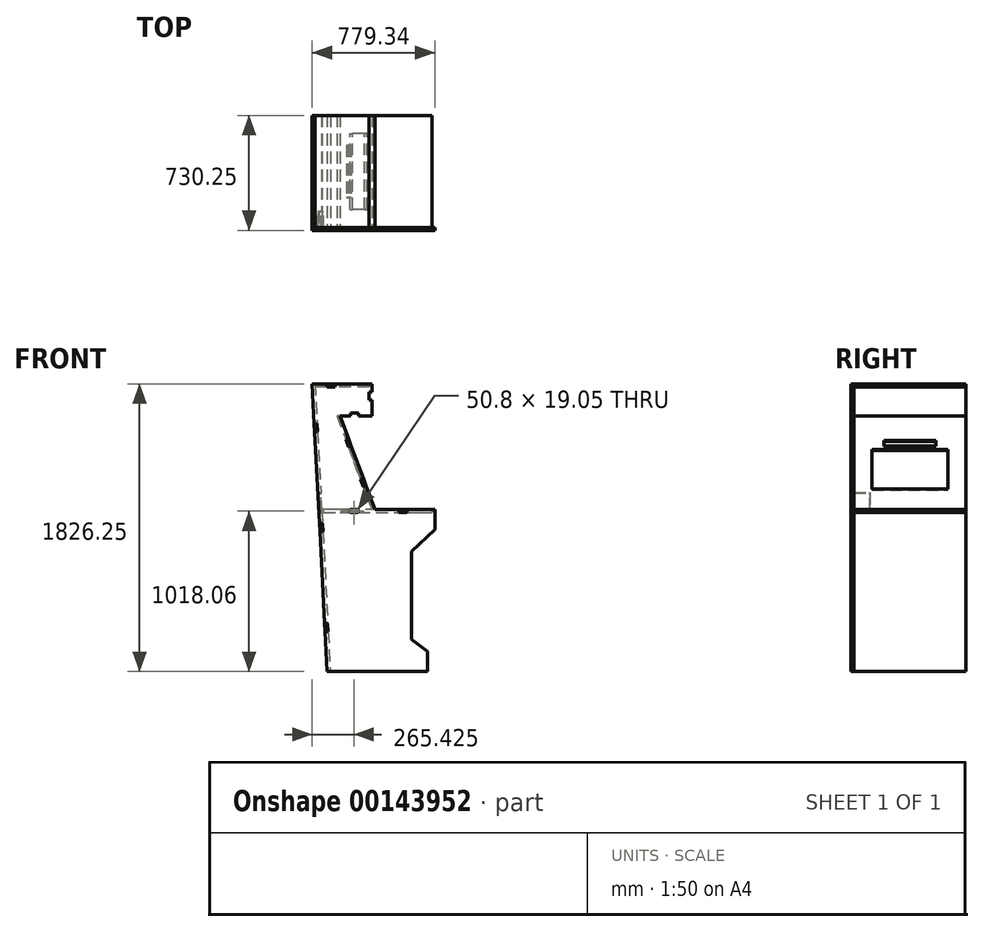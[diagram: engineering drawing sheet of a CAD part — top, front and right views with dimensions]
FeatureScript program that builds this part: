
annotation { "Feature Type Name" : "Feature", "Feature Type Description" : "" }
export const myFeature = defineFeature(function(context is Context, id is Id, definition is map)
    precondition{}
    {
        {
            var Q0;
            Q0=qCreatedBy(makeId("Front.planeOp"),FACE);
            var sketch = newSketch(context, id + "F0", { "sketchPlane" : qUnion([Q0])});
            skLineSegment(sketch, "E0.top", {"start": v(-166.11, 1576.37) * mm, "end": v(-343.91, 1576.37) * mm});
            skPoint(sketch, "E1.visualSharp", {"position": v(-407.41, 1576.37) * mm});
            skLineSegment(sketch, "E2", {"start": v(-247.51, -249.88) * mm, "end": v(387.49, -249.88) * mm});
            skLineSegment(sketch, "E3", {"start": v(387.49, -249.88) * mm, "end": v(387.49, -122.88) * mm});
            skLineSegment(sketch, "E4", {"start": v(387.49, -122.88) * mm, "end": v(286.3, -46.13) * mm});
            skLineSegment(sketch, "E5", {"start": v(286.3, -46.13) * mm, "end": v(286.3, 512.67) * mm});
            skLineSegment(sketch, "E6", {"start": v(286.3, 512.67) * mm, "end": v(435.43, 650.7) * mm});
            skLineSegment(sketch, "E7", {"start": v(435.43, 650.7) * mm, "end": v(435.43, 736.01) * mm});
            skLineSegment(sketch, "E8", {"start": v(435.43, 777.7) * mm, "end": v(54.43, 777.7) * mm});
            skLineSegment(sketch, "E9", {"start": v(54.43, 777.7) * mm, "end": v(-166.11, 1373.17) * mm});
            skLineSegment(sketch, "E10.bottom", {"start": v(-166.11, 1373.17) * mm, "end": v(37.09, 1373.17) * mm});
            skLineSegment(sketch, "E10.top", {"start": v(-166.11, 1576.37) * mm, "end": v(37.09, 1576.37) * mm});
            skLineSegment(sketch, "E10.right", {"start": v(37.09, 1373.17) * mm, "end": v(37.09, 1576.37) * mm});
            skLineSegment(sketch, "E11", {"start": v(-343.91, 1576.37) * mm, "end": v(-247.51, -249.88) * mm});
            skLineSegment(sketch, "E12", {"start": v(435.43, 736.01) * mm, "end": v(435.43, 777.7) * mm});
            skLineSegment(sketch, "E13", {"start": v(435.43, 650.7) * mm, "end": v(-295.05, 650.7) * mm, "construction": true});
            skSolve(sketch);
        }
        {
            var Q0;
            Q0=makeQuery(id+"F0.imprint","IMPRINT",FACE,{"disambiguationData":[TD([[makeQuery(id+"F0.imprint","IMPRINT",EDGE,{"derivedFrom":sQuery(id+"F0.wireOp",EDGE,"E0.top")}),1.0]])]});
            var sketch = newSketch(context, id + "F1", { "sketchPlane" : qUnion([Q0])});
            skSolve(sketch);
        }
        {
            var Q0;
            Q0=makeQuery(id+"F1.imprint","IMPRINT",FACE,{"disambiguationData":[TD([[makeQuery(id+"F1.imprint","IMPRINT",EDGE,{"derivedFrom":makeQuery(id+"F0.imprint","IMPRINT",EDGE,{"derivedFrom":sQuery(id+"F0.wireOp",EDGE,"E0.top")})}),1.0]])]});
            extrude(context, id + "F2", {"entities" : qUnion([Q0]), "depth" : 19.05 * mm});
        }
        {
            var Q0;
            Q0=makeQuery(id+"F0.imprint","IMPRINT",FACE,{"disambiguationData":[TD([[makeQuery(id+"F0.imprint","IMPRINT",EDGE,{"derivedFrom":sQuery(id+"F0.wireOp",EDGE,"E0.top")}),1.0]])]});
            var sketch = newSketch(context, id + "F3", { "sketchPlane" : qUnion([Q0])});
            skLineSegment(sketch, "E14.0.0", {"start": v(-58.16, 1576.37) * mm, "end": v(-108.96, 1576.37) * mm});
            skLineSegment(sketch, "E14.0.1", {"start": v(-196.83, 1576.37) * mm, "end": v(-247.63, 1576.37) * mm});
            skLineSegment(sketch, "E14.0.2", {"start": v(-330.53, 1322.73) * mm, "end": v(-327.85, 1272) * mm});
            skLineSegment(sketch, "E14.0.3", {"start": v(-247.51, -249.88) * mm, "end": v(387.49, -249.88) * mm});
            skLineSegment(sketch, "E14.0.4", {"start": v(387.49, -249.88) * mm, "end": v(387.49, -122.88) * mm});
            skLineSegment(sketch, "E14.0.5", {"start": v(387.49, -122.88) * mm, "end": v(286.3, -46.13) * mm});
            skLineSegment(sketch, "E14.0.6", {"start": v(286.3, -46.13) * mm, "end": v(286.3, 512.67) * mm});
            skLineSegment(sketch, "E14.0.7", {"start": v(286.3, 512.67) * mm, "end": v(435.43, 650.7) * mm});
            skLineSegment(sketch, "E14.0.8", {"start": v(435.43, 650.7) * mm, "end": v(435.43, 736.01) * mm});
            skLineSegment(sketch, "E14.0.9", {"start": v(435.43, 736.01) * mm, "end": v(435.43, 777.7) * mm});
            skLineSegment(sketch, "E14.0.10", {"start": v(257.63, 777.7) * mm, "end": v(206.83, 777.7) * mm});
            skLineSegment(sketch, "E14.0.11", {"start": v(-0.8, 926.82) * mm, "end": v(-18.44, 974.46) * mm});
            skLineSegment(sketch, "E14.0.12", {"start": v(-99.44, 1373.17) * mm, "end": v(-48.64, 1373.17) * mm});
            skLineSegment(sketch, "E14.0.13", {"start": v(37.09, 1474.77) * mm, "end": v(37.09, 1525.57) * mm});
            skPoint(sketch, "E15", {"position": v(18.04, 1557.32) * mm});
            skPoint(sketch, "E16", {"position": v(-323.83, 1557.32) * mm});
            skPoint(sketch, "E17", {"position": v(18.04, 1392.22) * mm});
            skPoint(sketch, "E18", {"position": v(-166.11, 1392.22) * mm});
            skPoint(sketch, "E19", {"position": v(-185.16, 1373.17) * mm});
            skPoint(sketch, "E20", {"position": v(35.38, 777.7) * mm});
            skPoint(sketch, "E21", {"position": v(-228.46, -249.88) * mm});
            skLineSegment(sketch, "E22", {"start": v(-323.83, 1557.32) * mm, "end": v(-228.46, -249.88) * mm, "construction": true});
            skLineSegment(sketch, "E23", {"start": v(-185.16, 1373.17) * mm, "end": v(35.38, 777.7) * mm, "construction": true});
            skLineSegment(sketch, "E24", {"start": v(18.04, 1557.32) * mm, "end": v(-323.83, 1557.32) * mm, "construction": true});
            skLineSegment(sketch, "E25", {"start": v(18.04, 1557.32) * mm, "end": v(18.04, 1392.22) * mm, "construction": true});
            skLineSegment(sketch, "E26", {"start": v(-166.11, 1392.22) * mm, "end": v(18.04, 1392.22) * mm, "construction": true});
            skLineSegment(sketch, "E27.top", {"start": v(-196.83, 1557.32) * mm, "end": v(-247.63, 1557.32) * mm});
            skLineSegment(sketch, "E27.left", {"start": v(-196.83, 1576.37) * mm, "end": v(-196.83, 1557.32) * mm});
            skLineSegment(sketch, "E27.right", {"start": v(-247.63, 1576.37) * mm, "end": v(-247.63, 1557.32) * mm});
            skLineSegment(sketch, "E28.bottom", {"start": v(-108.96, 1576.37) * mm, "end": v(-58.16, 1576.37) * mm});
            skLineSegment(sketch, "E28.top", {"start": v(-108.96, 1557.32) * mm, "end": v(-58.16, 1557.32) * mm});
            skLineSegment(sketch, "E28.left", {"start": v(-108.96, 1576.37) * mm, "end": v(-108.96, 1557.32) * mm});
            skLineSegment(sketch, "E28.right", {"start": v(-58.16, 1576.37) * mm, "end": v(-58.16, 1557.32) * mm});
            skLineSegment(sketch, "E29.bottom", {"start": v(-48.64, 1392.22) * mm, "end": v(-99.44, 1392.22) * mm});
            skLineSegment(sketch, "E29.top", {"start": v(-48.64, 1373.17) * mm, "end": v(-99.44, 1373.17) * mm});
            skLineSegment(sketch, "E29.left", {"start": v(-48.64, 1392.22) * mm, "end": v(-48.64, 1373.17) * mm});
            skLineSegment(sketch, "E29.right", {"start": v(-99.44, 1392.22) * mm, "end": v(-99.44, 1373.17) * mm});
            skLineSegment(sketch, "E30.bottom", {"start": v(37.09, 1525.57) * mm, "end": v(18.04, 1525.57) * mm});
            skLineSegment(sketch, "E30.top", {"start": v(37.09, 1474.77) * mm, "end": v(18.04, 1474.77) * mm});
            skLineSegment(sketch, "E30.left", {"start": v(37.09, 1525.57) * mm, "end": v(37.09, 1474.77) * mm});
            skLineSegment(sketch, "E30.right", {"start": v(18.04, 1525.57) * mm, "end": v(18.04, 1474.77) * mm});
            skPoint(sketch, "E31", {"position": v(-17.55, 920.61) * mm});
            skPoint(sketch, "E32", {"position": v(-35.2, 968.25) * mm});
            skPoint(sketch, "E33", {"position": v(-112.3, 1176.42) * mm});
            skPoint(sketch, "E34", {"position": v(-129.94, 1224.06) * mm});
            skLineSegment(sketch, "E35", {"start": v(-129.94, 1224.06) * mm, "end": v(-113.18, 1230.26) * mm});
            skLineSegment(sketch, "E36", {"start": v(-112.3, 1176.42) * mm, "end": v(-95.54, 1182.62) * mm});
            skLineSegment(sketch, "E37", {"start": v(-17.55, 920.61) * mm, "end": v(-0.8, 926.82) * mm});
            skLineSegment(sketch, "E38", {"start": v(-35.2, 968.25) * mm, "end": v(-18.44, 974.46) * mm});
            skLineSegment(sketch, "E39", {"start": v(-17.55, 920.61) * mm, "end": v(-35.2, 968.25) * mm});
            skLineSegment(sketch, "E40", {"start": v(-129.94, 1224.06) * mm, "end": v(-112.3, 1176.42) * mm});
            skPoint(sketch, "E41", {"position": v(-330.53, 1322.73) * mm});
            skPoint(sketch, "E42", {"position": v(-327.85, 1272) * mm});
            skPoint(sketch, "E43", {"position": v(-297.05, 688.6) * mm});
            skPoint(sketch, "E44", {"position": v(-294.38, 637.88) * mm});
            skPoint(sketch, "E45", {"position": v(-263.58, 54.5) * mm});
            skPoint(sketch, "E46", {"position": v(-260.9, 3.76) * mm});
            skLineSegment(sketch, "E47", {"start": v(-297.05, 688.6) * mm, "end": v(-278.04, 689.61) * mm});
            skLineSegment(sketch, "E48", {"start": v(-294.38, 637.88) * mm, "end": v(-275.37, 638.88) * mm});
            skLineSegment(sketch, "E49", {"start": v(-275.37, 638.88) * mm, "end": v(-278.04, 689.61) * mm});
            skLineSegment(sketch, "E50", {"start": v(-330.53, 1322.73) * mm, "end": v(-311.5, 1323.73) * mm});
            skLineSegment(sketch, "E51", {"start": v(-327.85, 1272) * mm, "end": v(-308.83, 1273) * mm});
            skLineSegment(sketch, "E52", {"start": v(-308.83, 1273) * mm, "end": v(-311.5, 1323.73) * mm});
            skLineSegment(sketch, "E53", {"start": v(-260.9, 3.76) * mm, "end": v(-241.9, 4.77) * mm});
            skLineSegment(sketch, "E54", {"start": v(-263.58, 54.5) * mm, "end": v(-244.58, 55.5) * mm});
            skLineSegment(sketch, "E55", {"start": v(-244.58, 55.5) * mm, "end": v(-241.9, 4.77) * mm});
            skLineSegment(sketch, "E56", {"start": v(514.5, 758.65) * mm, "end": v(-381.03, 758.65) * mm, "construction": true});
            skLineSegment(sketch, "E57.top", {"start": v(257.63, 758.65) * mm, "end": v(206.83, 758.65) * mm});
            skLineSegment(sketch, "E57.left", {"start": v(257.63, 777.7) * mm, "end": v(257.63, 758.65) * mm});
            skLineSegment(sketch, "E57.right", {"start": v(206.83, 777.7) * mm, "end": v(206.83, 758.65) * mm});
            skLineSegment(sketch, "E58.bottom", {"start": v(-103.89, 758.65) * mm, "end": v(-53.09, 758.65) * mm});
            skLineSegment(sketch, "E58.top", {"start": v(-103.89, 777.7) * mm, "end": v(-53.09, 777.7) * mm});
            skLineSegment(sketch, "E58.left", {"start": v(-103.89, 758.65) * mm, "end": v(-103.89, 777.7) * mm});
            skLineSegment(sketch, "E58.right", {"start": v(-53.09, 758.65) * mm, "end": v(-53.09, 777.7) * mm});
            skPoint(sketch, "E59", {"position": v(-281.69, 758.65) * mm});
            skLineSegment(sketch, "E60", {"start": v(-297.05, 688.6) * mm, "end": v(-294.38, 637.88) * mm});
            skPoint(sketch, "E61.orphan", {"position": v(54.43, 777.7) * mm});
            skLineSegment(sketch, "E62.trimOffspring", {"start": v(-95.54, 1182.62) * mm, "end": v(-113.18, 1230.26) * mm});
            skPoint(sketch, "E63.orphan", {"position": v(-166.11, 1373.17) * mm});
            skPoint(sketch, "E64.orphan", {"position": v(37.09, 1373.17) * mm});
            skPoint(sketch, "E65.orphan", {"position": v(37.09, 1576.37) * mm});
            skPoint(sketch, "E66.orphan", {"position": v(-166.11, 1576.37) * mm});
            skPoint(sketch, "E67.orphan", {"position": v(-343.91, 1576.37) * mm});
            skLineSegment(sketch, "E68.trimOffspring", {"start": v(-300.75, 758.65) * mm, "end": v(-294.38, 637.88) * mm});
            skLineSegment(sketch, "E69.trimOffspring", {"start": v(-263.58, 54.5) * mm, "end": v(-260.9, 3.76) * mm});
            skSolve(sketch);
        }
        {
            var Q0;
            Q0=makeQuery(id+"F3.imprint","IMPRINT",FACE,{"disambiguationData":[TD([[makeQuery(id+"F3.imprint","IMPRINT",EDGE,{"derivedFrom":sQuery(id+"F3.wireOp",EDGE,"E57.top")}),-1.0]])]});
            var Q1;
            Q1=makeQuery(id+"F3.imprint","IMPRINT",FACE,{"disambiguationData":[TD([[makeQuery(id+"F3.imprint","IMPRINT",EDGE,{"derivedFrom":sQuery(id+"F3.wireOp",EDGE,"E58.bottom")}),1.0]])]});
            var Q2;
            {var subQ0=sQuery(id+"F3.wireOp",EDGE,"E47");Q2=makeQuery(id+"F3.imprint","IMPRINT",FACE,{"disambiguationData":[TD([[makeQuery(id+"F3.imprint","IMPRINT",EDGE,{"derivedFrom":subQ0}),-1.0]])]});}
            var Q3;
            Q3=makeQuery(id+"F3.imprint","IMPRINT",FACE,{"disambiguationData":[TD([[makeQuery(id+"F3.imprint","IMPRINT",EDGE,{"derivedFrom":sQuery(id+"F3.wireOp",EDGE,"E14.0.11")}),1.0]])]});
            var Q4;
            Q4=makeQuery(id+"F3.imprint","IMPRINT",FACE,{"disambiguationData":[TD([[makeQuery(id+"F3.imprint","IMPRINT",EDGE,{"derivedFrom":sQuery(id+"F3.wireOp",EDGE,"E35")}),-1.0]])]});
            var Q5;
            Q5=makeQuery(id+"F3.imprint","IMPRINT",FACE,{"disambiguationData":[TD([[makeQuery(id+"F3.imprint","IMPRINT",EDGE,{"derivedFrom":sQuery(id+"F3.wireOp",EDGE,"E50")}),-1.0]])]});
            var Q6;
            Q6=makeQuery(id+"F3.imprint","IMPRINT",FACE,{"disambiguationData":[TD([[makeQuery(id+"F3.imprint","IMPRINT",EDGE,{"derivedFrom":sQuery(id+"F3.wireOp",EDGE,"E29.bottom")}),1.0]])]});
            var Q7;
            Q7=makeQuery(id+"F3.imprint","IMPRINT",FACE,{"disambiguationData":[TD([[makeQuery(id+"F3.imprint","IMPRINT",EDGE,{"derivedFrom":sQuery(id+"F3.wireOp",EDGE,"E30.bottom")}),1.0]])]});
            var Q8;
            Q8=makeQuery(id+"F3.imprint","IMPRINT",FACE,{"disambiguationData":[TD([[makeQuery(id+"F3.imprint","IMPRINT",EDGE,{"derivedFrom":sQuery(id+"F3.wireOp",EDGE,"E28.bottom")}),-1.0]])]});
            var Q9;
            Q9=makeQuery(id+"F3.imprint","IMPRINT",FACE,{"disambiguationData":[TD([[makeQuery(id+"F3.imprint","IMPRINT",EDGE,{"derivedFrom":sQuery(id+"F3.wireOp",EDGE,"E14.0.1")}),1.0]])]});
            var Q10;
            Q10=makeQuery(id+"F3.imprint","IMPRINT",FACE,{"disambiguationData":[TD([[makeQuery(id+"F3.imprint","IMPRINT",EDGE,{"derivedFrom":sQuery(id+"F3.wireOp",EDGE,"E53")}),1.0]])]});
            var Q11;
            Q11=makeQuery(id+"F2.opExtrude","CAP_FACE",FACE,{"disambiguationData":[OSD([sQuery(id+"F0.wireOp",EDGE,"E0.top"),sQuery(id+"F0.wireOp",EDGE,"E2"),sQuery(id+"F0.wireOp",EDGE,"E3"),sQuery(id+"F0.wireOp",EDGE,"E4"),sQuery(id+"F0.wireOp",EDGE,"E5"),sQuery(id+"F0.wireOp",EDGE,"E6"),sQuery(id+"F0.wireOp",EDGE,"E7"),sQuery(id+"F0.wireOp",EDGE,"E8"),sQuery(id+"F0.wireOp",EDGE,"E9"),sQuery(id+"F0.wireOp",EDGE,"E10.bottom"),sQuery(id+"F0.wireOp",EDGE,"E10.top"),sQuery(id+"F0.wireOp",EDGE,"E10.right"),sQuery(id+"F0.wireOp",EDGE,"E11"),sQuery(id+"F0.wireOp",EDGE,"E12")])],"isStart":false});
            extrude(context, id + "F4", {"entities" : qUnion([Q0, Q1, Q2, Q3, Q4, Q5, Q6, Q7, Q8, Q9, Q10]), "operationType" : NewBodyOperationType.REMOVE, "endBound" : BoundingType.UP_TO_SURFACE, "endBoundEntityFace" : qUnion([Q11]), "depth" : 19.05 * mm});
        }
        {
            var Q0;
            Q0=makeQuery(id+"F0.imprint","IMPRINT",FACE,{"disambiguationData":[TD([[makeQuery(id+"F0.imprint","IMPRINT",EDGE,{"derivedFrom":sQuery(id+"F0.wireOp",EDGE,"E0.top")}),1.0]])]});
            var sketch = newSketch(context, id + "F5", { "sketchPlane" : qUnion([Q0])});
            skLineSegment(sketch, "E70.0", {"start": v(-343.91, 1576.37) * mm, "end": v(-247.51, -249.88) * mm});
            skLineSegment(sketch, "E71.0", {"start": v(416.38, 777.7) * mm, "end": v(54.43, 777.7) * mm});
            skPoint(sketch, "E72", {"position": v(435.43, 758.65) * mm});
            skPoint(sketch, "E73", {"position": v(-301.76, 777.7) * mm});
            skPoint(sketch, "E74", {"position": v(-300.75, 758.65) * mm});
            skLineSegment(sketch, "E75", {"start": v(-301.76, 777.7) * mm, "end": v(-300.75, 758.65) * mm, "construction": true});
            skPoint(sketch, "E76", {"position": v(-282.7, 777.7) * mm});
            skPoint(sketch, "E77", {"position": v(-281.7, 758.65) * mm});
            skLineSegment(sketch, "E78", {"start": v(54.43, 777.7) * mm, "end": v(-282.7, 777.7) * mm});
            skLineSegment(sketch, "E79", {"start": v(-281.7, 758.65) * mm, "end": v(-282.7, 777.7) * mm});
            skLineSegment(sketch, "E80", {"start": v(-281.7, 758.65) * mm, "end": v(416.38, 758.65) * mm});
            skLineSegment(sketch, "E81", {"start": v(435.43, 777.7) * mm, "end": v(435.43, 758.65) * mm, "construction": true});
            skLineSegment(sketch, "E82", {"start": v(416.38, 777.7) * mm, "end": v(416.38, 758.65) * mm});
            skSolve(sketch);
        }
        {
            var Q0;
            Q0 = qSketchRegion(id + "F5", true);
            extrude(context, id + "F6", {"entities" : qUnion([Q0]), "oppositeDirection" : true, "depth" : 711.2 * mm});
        }
        {
            var Q0;
            Q0=makeQuery(id+"F6.opExtrude","SWEPT_FACE",FACE,{"disambiguationData":[OSD([sQuery(id+"F5.wireOp",EDGE,"E71.0"),sQuery(id+"F5.wireOp",EDGE,"E78")])]});
            var sketch = newSketch(context, id + "F7", { "sketchPlane" : qUnion([Q0])});
            skLineSegment(sketch, "E83.bottom", {"start": v(-282.7, 0) * mm, "end": v(-270, 0) * mm});
            skLineSegment(sketch, "E83.top", {"start": v(-282.7, 101.6) * mm, "end": v(-270, 101.6) * mm});
            skLineSegment(sketch, "E83.left", {"start": v(-282.7, 0) * mm, "end": v(-282.7, 101.6) * mm});
            skLineSegment(sketch, "E83.right", {"start": v(-270, 0) * mm, "end": v(-270, 101.6) * mm});
            skSolve(sketch);
        }
        {
            var Q0;
            Q0=makeQuery(id+"F7.imprint","IMPRINT",FACE,{"disambiguationData":[TD([[makeQuery(id+"F7.imprint","IMPRINT",EDGE,{"derivedFrom":sQuery(id+"F7.wireOp",EDGE,"E83.bottom")}),-1.0]])]});
            var Q1;
            Q1=makeQuery(id+"F6.opExtrude","SWEPT_FACE",FACE,{"disambiguationData":[OSD([sQuery(id+"F5.wireOp",EDGE,"E80")])]});
            extrude(context, id + "F8", {"entities" : qUnion([Q0]), "operationType" : NewBodyOperationType.REMOVE, "endBound" : BoundingType.UP_TO_SURFACE, "oppositeDirection" : true, "endBoundEntityFace" : qUnion([Q1]), "depth" : 25.4 * mm});
        }
        {
            var Q0;
            Q0=makeQuery(id+"F0.imprint","IMPRINT",FACE,{"disambiguationData":[TD([[makeQuery(id+"F0.imprint","IMPRINT",EDGE,{"derivedFrom":sQuery(id+"F0.wireOp",EDGE,"E0.top")}),1.0]])]});
            var sketch = newSketch(context, id + "F9", { "sketchPlane" : qUnion([Q0])});
            skLineSegment(sketch, "E84.0", {"start": v(-343.91, 1576.37) * mm, "end": v(-247.51, -249.88) * mm});
            skLineSegment(sketch, "E85.0", {"start": v(-166.11, 1576.37) * mm, "end": v(-343.91, 1576.37) * mm});
            skLineSegment(sketch, "E86.0", {"start": v(-247.51, -249.88) * mm, "end": v(387.49, -249.88) * mm});
            skLineSegment(sketch, "E87", {"start": v(-324.86, 1576.37) * mm, "end": v(-228.46, -249.88) * mm});
            skSolve(sketch);
        }
        {
            var Q0;
            Q0 = qSketchRegion(id + "F9", true);
            extrude(context, id + "F10", {"entities" : qUnion([Q0]), "oppositeDirection" : true, "depth" : 711.2 * mm});
        }
        {
            var Q0;
            Q0=makeQuery(id+"F10.opExtrude","SWEPT_FACE",FACE,{"disambiguationData":[OSD([sQuery(id+"F9.wireOp",EDGE,"E87")])]});
            var sketch = newSketch(context, id + "F11", { "sketchPlane" : qUnion([Q0])});
            skLineSegment(sketch, "E88.0.0", {"start": v(0, 1591.3) * mm, "end": v(0, -237.5) * mm});
            skLineSegment(sketch, "E88.0.1", {"start": v(0, -237.5) * mm, "end": v(711.2, -237.5) * mm});
            skLineSegment(sketch, "E88.0.2", {"start": v(711.2, -237.5) * mm, "end": v(711.2, 1591.3) * mm});
            skLineSegment(sketch, "E88.0.3", {"start": v(711.2, 1591.3) * mm, "end": v(0, 1591.3) * mm});
            skLineSegment(sketch, "E89.0", {"start": v(711.2, 772.45) * mm, "end": v(101.6, 772.45) * mm});
            skLineSegment(sketch, "E90.bottom", {"start": v(101.6, 772.45) * mm, "end": v(0, 772.45) * mm});
            skLineSegment(sketch, "E90.top", {"start": v(101.6, 899.45) * mm, "end": v(0, 899.45) * mm});
            skLineSegment(sketch, "E90.left", {"start": v(101.6, 772.45) * mm, "end": v(101.6, 899.45) * mm});
            skLineSegment(sketch, "E90.right", {"start": v(0, 772.45) * mm, "end": v(0, 899.45) * mm});
            skSolve(sketch);
        }
        {
            var Q0;
            Q0=makeQuery(id+"F11.imprint","IMPRINT",FACE,{"disambiguationData":[TD([[makeQuery(id+"F11.imprint","IMPRINT",EDGE,{"derivedFrom":sQuery(id+"F11.wireOp",EDGE,"E90.bottom")}),-1.0]])]});
            var Q1;
            Q1=makeQuery(id+"F10.opExtrude","SWEPT_FACE",FACE,{"disambiguationData":[OSD([sQuery(id+"F9.wireOp",EDGE,"E84.0")])]});
            extrude(context, id + "F12", {"entities" : qUnion([Q0]), "operationType" : NewBodyOperationType.REMOVE, "endBound" : BoundingType.UP_TO_SURFACE, "oppositeDirection" : true, "endBoundEntityFace" : qUnion([Q1]), "depth" : 25.4 * mm});
        }
        {
            var Q0;
            Q0=makeQuery(id+"F12.boolean.opBoolean","COPY",FACE,{"derivedFrom":makeQuery(id+"F12.opExtrude","SWEPT_FACE",FACE,{"disambiguationData":[OSD([sQuery(id+"F11.wireOp",EDGE,"E90.left")])]})});
            var sketch = newSketch(context, id + "F13", { "sketchPlane" : qUnion([Q0])});
            skLineSegment(sketch, "E91.bottom", {"start": v(-288.4, 885.48) * mm, "end": v(-307.4, 885.48) * mm});
            skLineSegment(sketch, "E91.top", {"start": v(-288.4, 884.47) * mm, "end": v(-307.4, 884.47) * mm});
            skLineSegment(sketch, "E91.left", {"start": v(-288.4, 885.48) * mm, "end": v(-288.4, 884.47) * mm});
            skLineSegment(sketch, "E91.right", {"start": v(-307.4, 885.48) * mm, "end": v(-307.4, 884.47) * mm});
            skLineSegment(sketch, "E92", {"start": v(-307.4, 885.48) * mm, "end": v(-301.75, 777.67) * mm});
            skLineSegment(sketch, "E93", {"start": v(-301.75, 777.67) * mm, "end": v(-282.76, 778.67) * mm});
            skLineSegment(sketch, "E94", {"start": v(-282.76, 778.67) * mm, "end": v(-288.4, 885.48) * mm});
            skSolve(sketch);
        }
        {
            var Q0;
            {var subQ1=sQuery(id+"F13.wireOp",EDGE,"E91.left");Q0=makeQuery(id+"F13.imprint","IMPRINT",FACE,{"disambiguationData":[TD([[makeQuery(id+"F13.imprint","IMPRINT",EDGE,{"derivedFrom":subQ1}),1.0]])]});}
            var Q1;
            Q1=makeQuery(id+"F2.opExtrude","SWEPT_BODY",BODY,{"disambiguationData":[OSD([sQuery(id+"F0.wireOp",EDGE,"E0.top"),sQuery(id+"F0.wireOp",EDGE,"E2"),sQuery(id+"F0.wireOp",EDGE,"E3"),sQuery(id+"F0.wireOp",EDGE,"E4"),sQuery(id+"F0.wireOp",EDGE,"E5"),sQuery(id+"F0.wireOp",EDGE,"E6"),sQuery(id+"F0.wireOp",EDGE,"E7"),sQuery(id+"F0.wireOp",EDGE,"E8"),sQuery(id+"F0.wireOp",EDGE,"E9"),sQuery(id+"F0.wireOp",EDGE,"E10.bottom"),sQuery(id+"F0.wireOp",EDGE,"E10.top"),sQuery(id+"F0.wireOp",EDGE,"E10.right"),sQuery(id+"F0.wireOp",EDGE,"E11"),sQuery(id+"F0.wireOp",EDGE,"E12")])]});
            extrude(context, id + "F14", {"entities" : qUnion([Q0]), "endBound" : BoundingType.UP_TO_BODY, "endBoundEntityBody" : qUnion([Q1]), "depth" : 25.4 * mm});
        }
        {
            var Q0;
            {var subQ2=sQuery(id+"F9.wireOp",EDGE,"E87");Q0=makeQuery(id+"F9.imprint","IMPRINT",FACE,{"disambiguationData":[TD([[makeQuery(id+"F9.imprint","IMPRINT",EDGE,{"derivedFrom":subQ2}),1.0]])]});}
            var sketch = newSketch(context, id + "F15", { "sketchPlane" : qUnion([Q0])});
            skLineSegment(sketch, "E95.0", {"start": v(-166.11, 1576.37) * mm, "end": v(18.04, 1576.37) * mm});
            skLineSegment(sketch, "E96.0", {"start": v(37.09, 1557.32) * mm, "end": v(37.09, 1576.37) * mm});
            skLineSegment(sketch, "E97.0", {"start": v(-166.11, 1576.37) * mm, "end": v(-324.86, 1576.37) * mm});
            skLineSegment(sketch, "E98.0", {"start": v(-324.86, 1576.37) * mm, "end": v(-228.46, -249.88) * mm});
            skPoint(sketch, "E99", {"position": v(37.09, 1557.32) * mm});
            skLineSegment(sketch, "E100", {"start": v(18.04, 1557.32) * mm, "end": v(-323.86, 1557.32) * mm});
            skLineSegment(sketch, "E101", {"start": v(-323.86, 1557.32) * mm, "end": v(-324.86, 1576.37) * mm});
            skPoint(sketch, "E102.orphan", {"position": v(37.09, 1373.17) * mm});
            skPoint(sketch, "E103.orphan", {"position": v(-343.91, 1576.37) * mm});
            skLineSegment(sketch, "E104", {"start": v(18.04, 1576.37) * mm, "end": v(18.04, 1557.32) * mm});
            skPoint(sketch, "E105.start.orphan", {"position": v(37.09, 1576.37) * mm});
            skSolve(sketch);
        }
        {
            var Q0;
            Q0=makeQuery(id+"F15.imprint","IMPRINT",FACE,{"disambiguationData":[TD([[makeQuery(id+"F15.imprint","IMPRINT",EDGE,{"derivedFrom":sQuery(id+"F15.wireOp",EDGE,"E95.0")}),-1.0]])]});
            extrude(context, id + "F16", {"entities" : qUnion([Q0]), "oppositeDirection" : true, "depth" : 711.2 * mm});
        }
        {
            var Q0;
            {var subQ2=sQuery(id+"F9.wireOp",EDGE,"E87");Q0=makeQuery(id+"F9.imprint","IMPRINT",FACE,{"disambiguationData":[TD([[makeQuery(id+"F9.imprint","IMPRINT",EDGE,{"derivedFrom":subQ2}),1.0]])]});}
            var sketch = newSketch(context, id + "F17", { "sketchPlane" : qUnion([Q0])});
            skLineSegment(sketch, "E106.0", {"start": v(54.43, 777.7) * mm, "end": v(-166.11, 1373.17) * mm});
            skLineSegment(sketch, "E107.0", {"start": v(54.43, 777.7) * mm, "end": v(35.38, 777.7) * mm});
            skPoint(sketch, "E108", {"position": v(-185.16, 1373.17) * mm});
            skPoint(sketch, "E109", {"position": v(35.38, 777.7) * mm});
            skLineSegment(sketch, "E110", {"start": v(-166.11, 1373.17) * mm, "end": v(-185.16, 1373.17) * mm});
            skLineSegment(sketch, "E111", {"start": v(-185.16, 1373.17) * mm, "end": v(35.38, 777.7) * mm});
            skPoint(sketch, "E112.orphan", {"position": v(-282.7, 777.7) * mm});
            skSolve(sketch);
        }
        {
            var Q0;
            Q0=makeQuery(id+"F17.imprint","IMPRINT",FACE,{"disambiguationData":[TD([[makeQuery(id+"F17.imprint","IMPRINT",EDGE,{"derivedFrom":sQuery(id+"F17.wireOp",EDGE,"E106.0")}),1.0]])]});
            extrude(context, id + "F18", {"entities" : qUnion([Q0]), "oppositeDirection" : true, "depth" : 711.2 * mm});
        }
        {
            var Q0;
            Q0=makeQuery(id+"F18.opExtrude","SWEPT_FACE",FACE,{"disambiguationData":[OSD([sQuery(id+"F17.wireOp",EDGE,"E106.0")])]});
            var sketch = newSketch(context, id + "F19", { "sketchPlane" : qUnion([Q0])});
            skLineSegment(sketch, "E113.0.0", {"start": v(0, 1345.39) * mm, "end": v(0, 710.39) * mm});
            skLineSegment(sketch, "E113.0.1", {"start": v(0, 710.39) * mm, "end": v(711.2, 710.39) * mm});
            skLineSegment(sketch, "E113.0.2", {"start": v(711.2, 710.39) * mm, "end": v(711.2, 1345.39) * mm});
            skLineSegment(sketch, "E113.0.3", {"start": v(711.2, 1345.39) * mm, "end": v(0, 1345.39) * mm});
            skLineSegment(sketch, "E114", {"start": v(-227.24, 850.09) * mm, "end": v(1021.03, 850.09) * mm, "construction": true});
            skPoint(sketch, "E115", {"position": v(355.6, 850.09) * mm});
            skPoint(sketch, "E115.positionSnap0", {"position": v(355.6, 1345.39) * mm});
            skPoint(sketch, "E116", {"position": v(596.9, 850.09) * mm});
            skPoint(sketch, "E117", {"position": v(114.3, 850.09) * mm});
            skLineSegment(sketch, "E118.bottom", {"start": v(114.3, 850.09) * mm, "end": v(596.9, 850.09) * mm});
            skLineSegment(sketch, "E118.top", {"start": v(114.3, 1116.79) * mm, "end": v(596.9, 1116.79) * mm});
            skLineSegment(sketch, "E118.left", {"start": v(114.3, 850.09) * mm, "end": v(114.3, 1116.79) * mm});
            skLineSegment(sketch, "E118.right", {"start": v(596.9, 850.09) * mm, "end": v(596.9, 1116.79) * mm});
            skLineSegment(sketch, "E119", {"start": v(-154.55, 1142.19) * mm, "end": v(954.4, 1142.19) * mm, "construction": true});
            skPoint(sketch, "E120", {"position": v(355.6, 1142.19) * mm});
            skPoint(sketch, "E121", {"position": v(520.7, 1142.19) * mm});
            skLineSegment(sketch, "E122.bottom", {"start": v(520.7, 1142.19) * mm, "end": v(190.5, 1142.19) * mm});
            skLineSegment(sketch, "E122.top", {"start": v(520.7, 1180.29) * mm, "end": v(190.5, 1180.29) * mm});
            skLineSegment(sketch, "E122.left", {"start": v(520.7, 1142.19) * mm, "end": v(520.7, 1180.29) * mm});
            skLineSegment(sketch, "E122.right", {"start": v(190.5, 1142.19) * mm, "end": v(190.5, 1180.29) * mm});
            skSolve(sketch);
        }
        {
            var Q0;
            Q0=makeQuery(id+"F19.imprint","IMPRINT",FACE,{"disambiguationData":[TD([[makeQuery(id+"F19.imprint","IMPRINT",EDGE,{"derivedFrom":sQuery(id+"F19.wireOp",EDGE,"E118.bottom")}),1.0]])]});
            var Q1;
            Q1=makeQuery(id+"F19.imprint","IMPRINT",FACE,{"disambiguationData":[TD([[makeQuery(id+"F19.imprint","IMPRINT",EDGE,{"derivedFrom":sQuery(id+"F19.wireOp",EDGE,"E122.bottom")}),-1.0]])]});
            var Q2;
            Q2=makeQuery(id+"F18.opExtrude","SWEPT_FACE",FACE,{"disambiguationData":[OSD([sQuery(id+"F17.wireOp",EDGE,"E111")])]});
            extrude(context, id + "F20", {"entities" : qUnion([Q0, Q1]), "operationType" : NewBodyOperationType.REMOVE, "endBound" : BoundingType.UP_TO_SURFACE, "oppositeDirection" : true, "endBoundEntityFace" : qUnion([Q2]), "depth" : 25.4 * mm});
        }
    });
